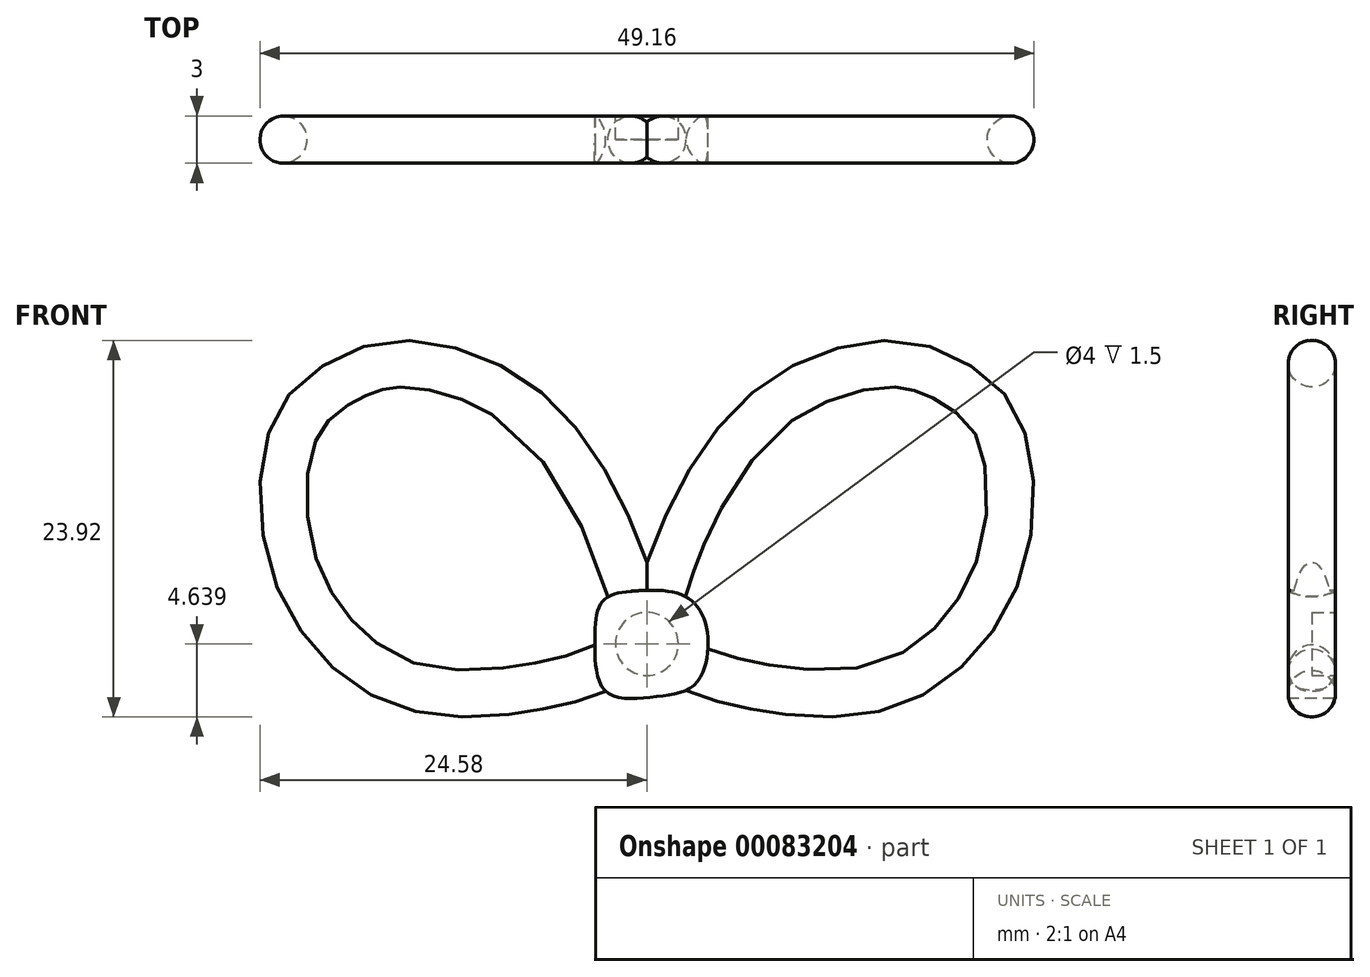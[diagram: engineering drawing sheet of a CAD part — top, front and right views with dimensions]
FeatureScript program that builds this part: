
annotation { "Feature Type Name" : "Feature", "Feature Type Description" : "" }
export const myFeature = defineFeature(function(context is Context, id is Id, definition is map)
    precondition{}
    {
        {
            var Q0;
            Q0=qCreatedBy(makeId("Front.planeOp"),FACE);
            var sketch = newSketch(context, id + "F0", { "sketchPlane" : qUnion([Q0])});
            skFitSpline(sketch, "E0", {"points": [v(0.8, 1.55) * mm, v(3.25, 8.24) * mm, v(8.68, 14.85) * mm, v(15.52, 17.06) * mm, v(18.99, 16.11) * mm, v(21.98, 13.6) * mm, v(23.08, 8) * mm, v(21.35, 1.87) * mm, v(16.31, -2.93) * mm, v(8.76, -3.72) * mm, v(1.51, -1.36) * mm, v(0.8, 1.55) * mm]});
            skSolve(sketch);
        }
        {
            var Q0;
            Q0=qCreatedBy(makeId("Top.planeOp"),FACE);
            var Q1;
            Q1=sQuery(id+"F0.wireOp",VERTEX,"E0.0.internal");
            cPlane(context, id + "F1", {"entities" : qUnion([Q0, Q1]), "cplaneType" : CPlaneType.PLANE_POINT, "offset" : 150 * mm, "width" : 150 * mm, "height" : 150 * mm});
        }
        {
            var Q0;
            Q0=qCreatedBy(id+"F1.planeOp",FACE);
            var sketch = newSketch(context, id + "F2", { "sketchPlane" : qUnion([Q0])});
            skPoint(sketch, "E1.0", {"position": v(0.8, 0) * mm});
            skCircle(sketch, "E2", {"center": v(0.8, 0) * mm, "radius": 1.5 * mm});
            skSolve(sketch);
        }
        {
            var Q0;
            Q0=makeQuery(id+"F2.imprint","IMPRINT",FACE,{"disambiguationData":[TD([[makeQuery(id+"F2.imprint","IMPRINT",EDGE,{"derivedFrom":sQuery(id+"F2.wireOp",EDGE,"E2")}),1.0]])]});
            var Q1;
            Q1=sQuery(id+"F0.wireOp",EDGE,"E0");
            sweep(context, id + "F3", {"profiles" : qUnion([Q0]), "path" : qUnion([Q1])});
        }
        {
            var Q0;
            Q0=makeQuery(id+"F3.opSweep","SWEPT_BODY",BODY,{"disambiguationData":[OSD([sQuery(id+"F0.wireOp",EDGE,"E0"),sQuery(id+"F2.wireOp",EDGE,"E2")])]});
            var Q1;
            Q1=qCreatedBy(makeId("Right.planeOp"),FACE);
            mirror(context, id + "F4", {"operationType" : NewBodyOperationType.ADD, "entities" : qUnion([Q0]), "mirrorPlane" : qUnion([Q1])});
        }
        {
            var Q0;
            Q0=qCreatedBy(makeId("Front.planeOp"),FACE);
            var sketch = newSketch(context, id + "F5", { "sketchPlane" : qUnion([Q0])});
            skFitSpline(sketch, "E3", {"points": [v(-2.79, 2) * mm, v(-0.68, 2.63) * mm, v(2.47, 2.26) * mm, v(3.83, 0) * mm, v(3.15, -3.2) * mm, v(0.58, -4.1) * mm, v(-2.58, -3.78) * mm, v(-3.31, -0.63) * mm, v(-2.79, 2) * mm]});
            skSolve(sketch);
        }
        {
            var Q0;
            Q0=makeQuery(id+"F5.imprint","IMPRINT",FACE,{"disambiguationData":[TD([[makeQuery(id+"F5.imprint","IMPRINT",EDGE,{"derivedFrom":sQuery(id+"F5.wireOp",EDGE,"E3")}),-1.0]])]});
            extrude(context, id + "F6", {"entities" : qUnion([Q0]), "operationType" : NewBodyOperationType.ADD, "endBound" : BoundingType.SYMMETRIC, "depth" : 3 * mm});
        }
        {
            var Q0;
            Q0=makeQuery(id+"F6.opExtrude","CAP_FACE",FACE,{"disambiguationData":[OSD([sQuery(id+"F5.wireOp",EDGE,"E3")])],"isStart":true});
            var sketch = newSketch(context, id + "F7", { "sketchPlane" : qUnion([Q0])});
            skLineSegment(sketch, "E4", {"start": v(0, 0) * mm, "end": v(0, -1.48) * mm});
            skCircle(sketch, "E5", {"center": v(0, -0.74) * mm, "radius": 2 * mm});
            skSolve(sketch);
        }
        {
            var Q0;
            Q0 = qSketchRegion(id + "F7", true);
            extrude(context, id + "F8", {"entities" : qUnion([Q0]), "operationType" : NewBodyOperationType.REMOVE, "oppositeDirection" : true, "depth" : 1.5 * mm});
        }
    });
